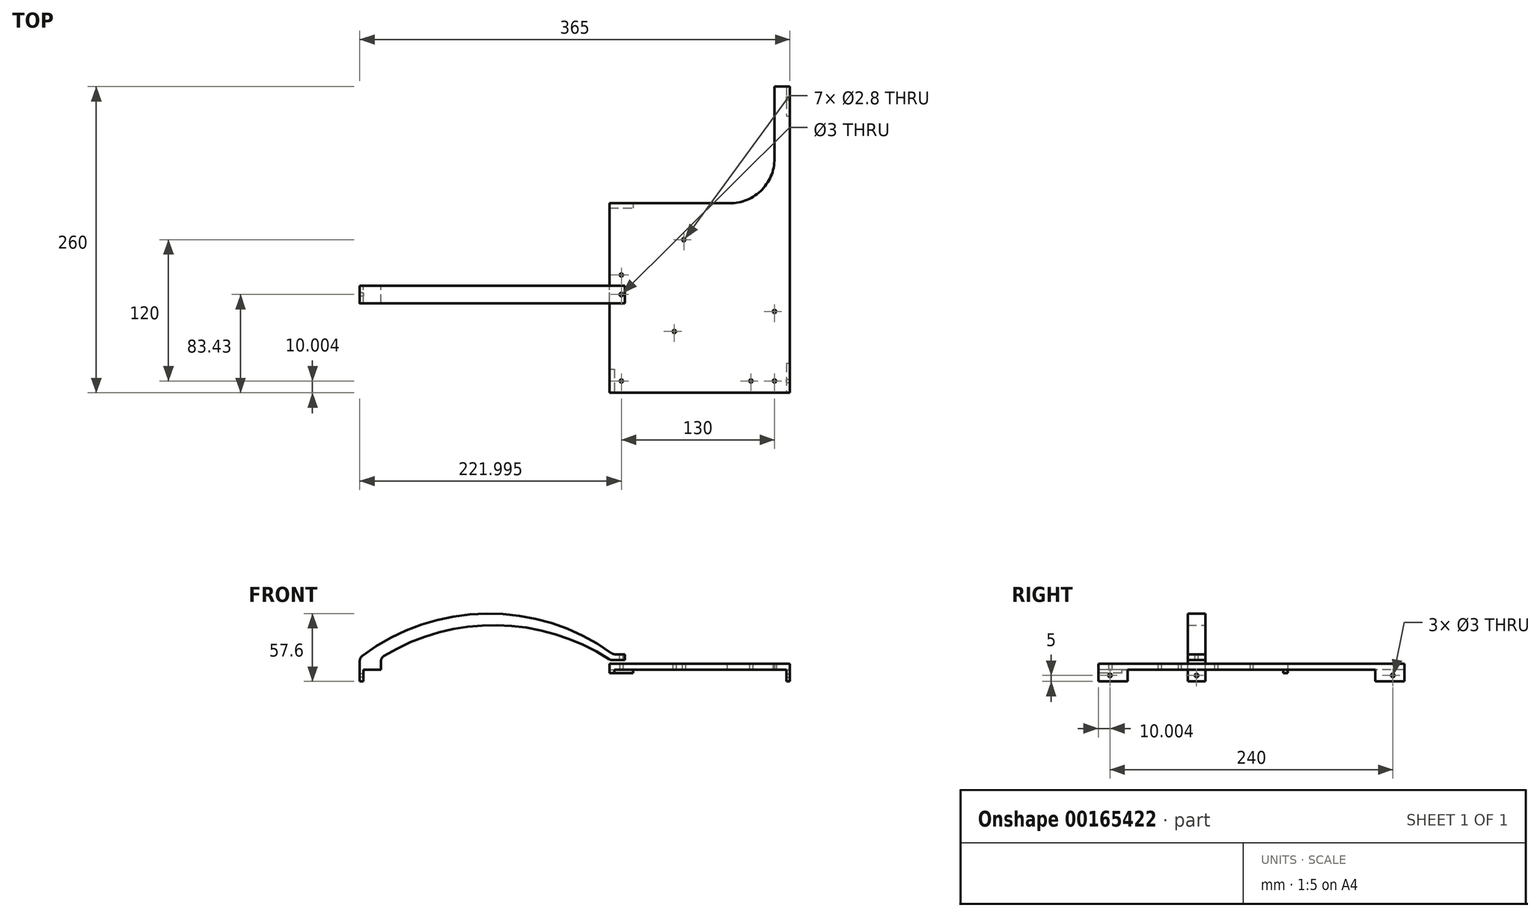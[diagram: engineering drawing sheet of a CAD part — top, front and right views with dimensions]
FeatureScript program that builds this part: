
annotation { "Feature Type Name" : "Feature", "Feature Type Description" : "" }
export const myFeature = defineFeature(function(context is Context, id is Id, definition is map)
    precondition{}
    {
        {
            var Q0;
            Q0=qCreatedBy(makeId("Top.planeOp"),FACE);
            var sketch = newSketch(context, id + "F0", { "sketchPlane" : qUnion([Q0])});
            skLineSegment(sketch, "E0", {"start": v(260.3, 169.07) * mm, "end": v(260.3, -90.93) * mm});
            skLineSegment(sketch, "E1", {"start": v(260.3, -90.93) * mm, "end": v(110.3, -90.93) * mm});
            skLineSegment(sketch, "E2", {"start": v(110.3, -90.93) * mm, "end": v(110.3, 70) * mm});
            skLineSegment(sketch, "E3", {"start": v(250.3, 169.07) * mm, "end": v(260.3, 169.07) * mm});
            skLineSegment(sketch, "E4", {"start": v(250.3, 169.07) * mm, "end": v(250.3, 107.94) * mm});
            skLineSegment(sketch, "E5", {"start": v(110.3, 70) * mm, "end": v(210.05, 70) * mm});
            skArc(sketch, "E6", {"start": v(250.3, 107.94) * mm, "mid": v(238.37, 80.28) * mm, "end": v(210.05, 70) * mm});
            skCircle(sketch, "E7", {"center": v(120.3, -80.93) * mm, "radius": 1.4 * mm});
            skCircle(sketch, "E8", {"center": v(230.3, -80.93) * mm, "radius": 1.4 * mm});
            skCircle(sketch, "E9", {"center": v(250.3, -80.93) * mm, "radius": 1.4 * mm});
            skCircle(sketch, "E10", {"center": v(250.3, -21.93) * mm, "radius": 1.4 * mm});
            skCircle(sketch, "E11", {"center": v(165.3, -38.93) * mm, "radius": 1.4 * mm});
            skCircle(sketch, "E12", {"center": v(120.3, 9.07) * mm, "radius": 1.4 * mm});
            skCircle(sketch, "E13", {"center": v(173.3, 39.07) * mm, "radius": 1.4 * mm});
            skSolve(sketch);
        }
        {
            var Q0;
            Q0 = qSketchRegion(id + "F0", true);
            extrude(context, id + "F1", {"entities" : qUnion([Q0]), "depth" : 5 * mm});
        }
        {
            var Q0;
            Q0=qCreatedBy(makeId("Top.planeOp"),FACE);
            var sketch = newSketch(context, id + "F2", { "sketchPlane" : qUnion([Q0])});
            skLineSegment(sketch, "E14.bottom", {"start": v(260.3, 169.07) * mm, "end": v(263.3, 169.07) * mm});
            skLineSegment(sketch, "E14.top", {"start": v(260.3, -90.93) * mm, "end": v(263.3, -90.93) * mm});
            skLineSegment(sketch, "E14.left", {"start": v(260.3, 169.07) * mm, "end": v(260.3, -90.93) * mm});
            skLineSegment(sketch, "E14.right", {"start": v(263.3, 169.07) * mm, "end": v(263.3, -90.93) * mm});
            skLineSegment(sketch, "E15.bottom", {"start": v(110.3, -70.93) * mm, "end": v(114.3, -70.93) * mm});
            skLineSegment(sketch, "E15.top", {"start": v(110.3, -90.93) * mm, "end": v(114.3, -90.93) * mm});
            skLineSegment(sketch, "E15.left", {"start": v(110.3, -70.93) * mm, "end": v(110.3, -90.93) * mm});
            skLineSegment(sketch, "E15.right", {"start": v(114.3, -70.93) * mm, "end": v(114.3, -90.93) * mm});
            skLineSegment(sketch, "E16.bottom", {"start": v(110.3, 70) * mm, "end": v(130.3, 70) * mm});
            skLineSegment(sketch, "E16.top", {"start": v(110.3, 66) * mm, "end": v(130.3, 66) * mm});
            skLineSegment(sketch, "E16.left", {"start": v(110.3, 70) * mm, "end": v(110.3, 66) * mm});
            skLineSegment(sketch, "E16.right", {"start": v(130.3, 70) * mm, "end": v(130.3, 66) * mm});
            skSolve(sketch);
        }
        {
            var Q0;
            Q0 = qSketchRegion(id + "F2", true);
            extrude(context, id + "F3", {"entities" : qUnion([Q0]), "operationType" : NewBodyOperationType.ADD, "depth" : 5 * mm});
        }
        {
            var Q0;
            Q0=makeQuery(id+"F2.imprint","IMPRINT",FACE,{"disambiguationData":[TD([[makeQuery(id+"F2.imprint","IMPRINT",EDGE,{"derivedFrom":sQuery(id+"F2.wireOp",EDGE,"E14.bottom")}),-1.0]])]});
            extrude(context, id + "F4", {"entities" : qUnion([Q0]), "operationType" : NewBodyOperationType.ADD, "oppositeDirection" : true, "depth" : 10 * mm});
        }
        {
            var Q0;
            {var subQ0=sQuery(id+"F2.wireOp",EDGE,"E14.right");Q0=makeQuery(id+"F4.boolean.opBoolean","MERGE",FACE,{"derivedFrom":[makeQuery(id+"F3.opExtrude","SWEPT_FACE",FACE,{"disambiguationData":[OSD([subQ0])]}),makeQuery(id+"F4.opExtrude","SWEPT_FACE",FACE,{"disambiguationData":[OSD([subQ0])]})]});}
            var sketch = newSketch(context, id + "F5", { "sketchPlane" : qUnion([Q0])});
            skCircle(sketch, "E17", {"center": v(-80.93, -5) * mm, "radius": 1.5 * mm});
            skCircle(sketch, "E18", {"center": v(159.07, -5) * mm, "radius": 1.5 * mm});
            skLineSegment(sketch, "E19.bottom", {"start": v(-65.93, -10) * mm, "end": v(144.07, -10) * mm});
            skLineSegment(sketch, "E19.top", {"start": v(-65.93, 0) * mm, "end": v(144.07, 0) * mm});
            skLineSegment(sketch, "E19.left", {"start": v(-65.93, -10) * mm, "end": v(-65.93, 0) * mm});
            skLineSegment(sketch, "E19.right", {"start": v(144.07, -10) * mm, "end": v(144.07, 0) * mm});
            skSolve(sketch);
        }
        {
            var Q0;
            Q0 = qSketchRegion(id + "F5", true);
            extrude(context, id + "F6", {"entities" : qUnion([Q0]), "operationType" : NewBodyOperationType.REMOVE, "oppositeDirection" : true, "depth" : 3 * mm});
        }
        {
            var Q0;
            Q0=makeQuery(id+"F2.imprint","IMPRINT",FACE,{"disambiguationData":[TD([[makeQuery(id+"F2.imprint","IMPRINT",EDGE,{"derivedFrom":sQuery(id+"F2.wireOp",EDGE,"E15.bottom")}),-1.0]])]});
            var Q1;
            Q1=makeQuery(id+"F2.imprint","IMPRINT",FACE,{"disambiguationData":[TD([[makeQuery(id+"F2.imprint","IMPRINT",EDGE,{"derivedFrom":sQuery(id+"F2.wireOp",EDGE,"E16.bottom")}),-1.0]])]});
            extrude(context, id + "F7", {"entities" : qUnion([Q0, Q1]), "operationType" : NewBodyOperationType.ADD, "oppositeDirection" : true, "depth" : 3 * mm});
        }
        {
            var Q0;
            Q0=qCreatedBy(makeId("Front.planeOp"),FACE);
            var sketch = newSketch(context, id + "F8", { "sketchPlane" : qUnion([Q0])});
            skLineSegment(sketch, "E20", {"start": v(-101.7, 10) * mm, "end": v(-101.7, -10) * mm});
            skLineSegment(sketch, "E21", {"start": v(-101.7, -10) * mm, "end": v(-98.7, -10) * mm});
            skLineSegment(sketch, "E22", {"start": v(-98.7, -10) * mm, "end": v(-98.7, 0) * mm});
            skLineSegment(sketch, "E23", {"start": v(-98.7, 0) * mm, "end": v(-83.7, 0) * mm});
            skLineSegment(sketch, "E24", {"start": v(-83.7, 0) * mm, "end": v(-83.7, 10) * mm});
            skArc(sketch, "E25", {"start": v(111.3, 8) * mm, "mid": v(14.1, 37.7) * mm, "end": v(-83.7, 10) * mm});
            skLineSegment(sketch, "E26", {"start": v(111.3, 8) * mm, "end": v(123.3, 8) * mm});
            skLineSegment(sketch, "E27", {"start": v(123.3, 8) * mm, "end": v(123.3, 13) * mm});
            skLineSegment(sketch, "E28", {"start": v(123.3, 13) * mm, "end": v(113.3, 13) * mm});
            skArc(sketch, "E29", {"start": v(113.3, 13) * mm, "mid": v(5.3, 47.58) * mm, "end": v(-101.7, 10) * mm});
            skSolve(sketch);
        }
        {
            var Q0;
            Q0 = qSketchRegion(id + "F8", true);
            extrude(context, id + "F9", {"entities" : qUnion([Q0]), "depth" : 15 * mm});
        }
        {
            var Q0;
            Q0=makeQuery(id+"F9.opExtrude","SWEPT_FACE",FACE,{"disambiguationData":[OSD([sQuery(id+"F8.wireOp",EDGE,"E20")])]});
            var sketch = newSketch(context, id + "F10", { "sketchPlane" : qUnion([Q0])});
            skCircle(sketch, "E30", {"center": v(7.5, -5) * mm, "radius": 1.5 * mm});
            skSolve(sketch);
        }
        {
            var Q0;
            Q0 = qSketchRegion(id + "F10", true);
            extrude(context, id + "F11", {"entities" : qUnion([Q0]), "operationType" : NewBodyOperationType.REMOVE, "oppositeDirection" : true, "depth" : 3 * mm});
        }
        {
            var Q0;
            Q0=makeQuery(id+"F9.opExtrude","SWEPT_FACE",FACE,{"disambiguationData":[OSD([sQuery(id+"F8.wireOp",EDGE,"E28")])]});
            var sketch = newSketch(context, id + "F12", { "sketchPlane" : qUnion([Q0])});
            skCircle(sketch, "E31", {"center": v(120.3, -7.5) * mm, "radius": 1.5 * mm});
            skSolve(sketch);
        }
        {
            var Q0;
            Q0 = qSketchRegion(id + "F12", true);
            extrude(context, id + "F13", {"entities" : qUnion([Q0]), "operationType" : NewBodyOperationType.REMOVE, "oppositeDirection" : true, "depth" : 5 * mm});
        }
        {
            var Q0;
            Q0=makeQuery(id+"F9.opExtrude","SWEPT_EDGE",EDGE,{"disambiguationData":[OSD([sQuery(id+"F8.wireOp",EDGE,"E24"),sQuery(id+"F8.wireOp",EDGE,"E25")])]});
            var Q1;
            Q1=makeQuery(id+"F9.opExtrude","SWEPT_EDGE",EDGE,{"disambiguationData":[OSD([sQuery(id+"F8.wireOp",EDGE,"E28"),sQuery(id+"F8.wireOp",EDGE,"E29")])]});
            var Q2;
            Q2=makeQuery(id+"F9.opExtrude","SWEPT_EDGE",EDGE,{"disambiguationData":[OSD([sQuery(id+"F8.wireOp",EDGE,"E25"),sQuery(id+"F8.wireOp",EDGE,"E26")])]});
            var Q3;
            Q3=makeQuery(id+"F9.opExtrude","SWEPT_EDGE",EDGE,{"disambiguationData":[OSD([sQuery(id+"F8.wireOp",EDGE,"E20"),sQuery(id+"F8.wireOp",EDGE,"E29")])]});
            fillet(context, id + "F14", {"entities" : qUnion([Q0, Q1, Q2, Q3]), "radius" : 5 * mm, "tangentPropagation" : true, "allowEdgeOverflow" : false});
        }
    });
